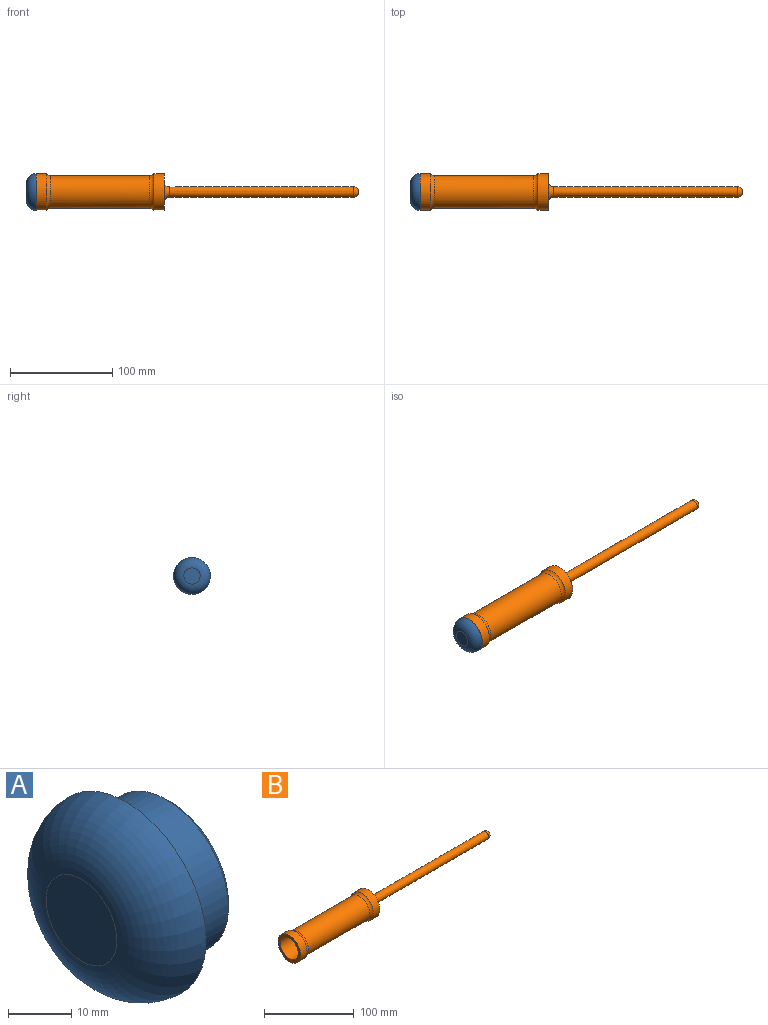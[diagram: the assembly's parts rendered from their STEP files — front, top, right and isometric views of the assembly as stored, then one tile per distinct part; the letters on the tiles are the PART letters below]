
ASSEMBLY  parts=2 mates=1
PART A: 9 faces, bbox 20x35.9x35.9 mm
  f0: plane 15.9x15.9mm, normal (-1,0,0), area 198.6mm2, adj f8
  f1: plane 35.9x35.9mm, normal (1,0,0), area 400.9mm2, adj f3,f8
  f2: cylinder r=11.45mm len=22.9mm, axis (-1,0,0), area 647.5mm2, adj f5,f6
  f3: cylinder r=13.95mm len=27.9mm, axis (-1,0,0), area 788.9mm2, adj f1,f7
  f4: plane 25.9x25.9mm, normal (1,0,0), area 39.9mm2, adj f6,f7
  f5: plane 22.9x22.9mm, normal (1,0,0), area 411.9mm2, adj f2
  f6: cone r=11.45mm half-angle=45deg, axis (1,0,0), area 106.2mm2, adj f2,f4
  f7: cone r=12.95mm half-angle=45deg, axis (-1,0,0), area 119.5mm2, adj f3,f4
  f8: torus R=7.95mm, axis (1,0,0), area 1413mm2, adj f0,f1
PART B: 13 faces, bbox 314.3x45.4x45.4 mm
  f0: cone r=5mm half-angle=0deg, axis (-1,0,0), area 5683.2mm2, adj f6,f7
  f1: plane 35.9x35.9mm, normal (1,0,0), area 695mm2, adj f2,f7
  f2: cylinder r=17.95mm len=35.9mm, axis (-1,0,0), area 1127.8mm2, adj f1,f8
  f3: cylinder r=15.95mm len=97mm, axis (-1,0,0), area 9721mm2, adj f8,f9
  f4: cylinder r=17.95mm len=35.9mm, axis (-1,0,0), area 1127.8mm2, adj f5,f9
  f5: plane 35.9x35.9mm, normal (-1,0,0), area 400.9mm2, adj f4,f10
  f6: torus R=0mm, axis (-1,0,0), area 136.1mm2, adj f0,f12
  f7: torus R=10.05mm, axis (1,0,0), area 338.8mm2, adj f0,f1
  f8: torus R=20.95mm, axis (1,0,0), area 484.6mm2, adj f2,f3
  f9: torus R=20.95mm, axis (-1,0,0), area 484.6mm2, adj f3,f4
  f10: cylinder r=13.95mm len=120mm, axis (-1,0,0), area 10518.1mm2, adj f5,f11
  f11: plane 27.9x27.9mm, normal (-1,0,0), area 591.7mm2, adj f10,f12
  f12: cylinder r=2.5mm len=194.33mm, axis (-1,0,0), area 3052.5mm2, adj f6,f11
PLACE A t=(0,-0.05,-10.89)mm
PLACE B t=(0,-15,55.37)mm
MATE slider B.f0 <-> A.f2  axis (-1,0,0) through (0,-0.05,55.37)mm
